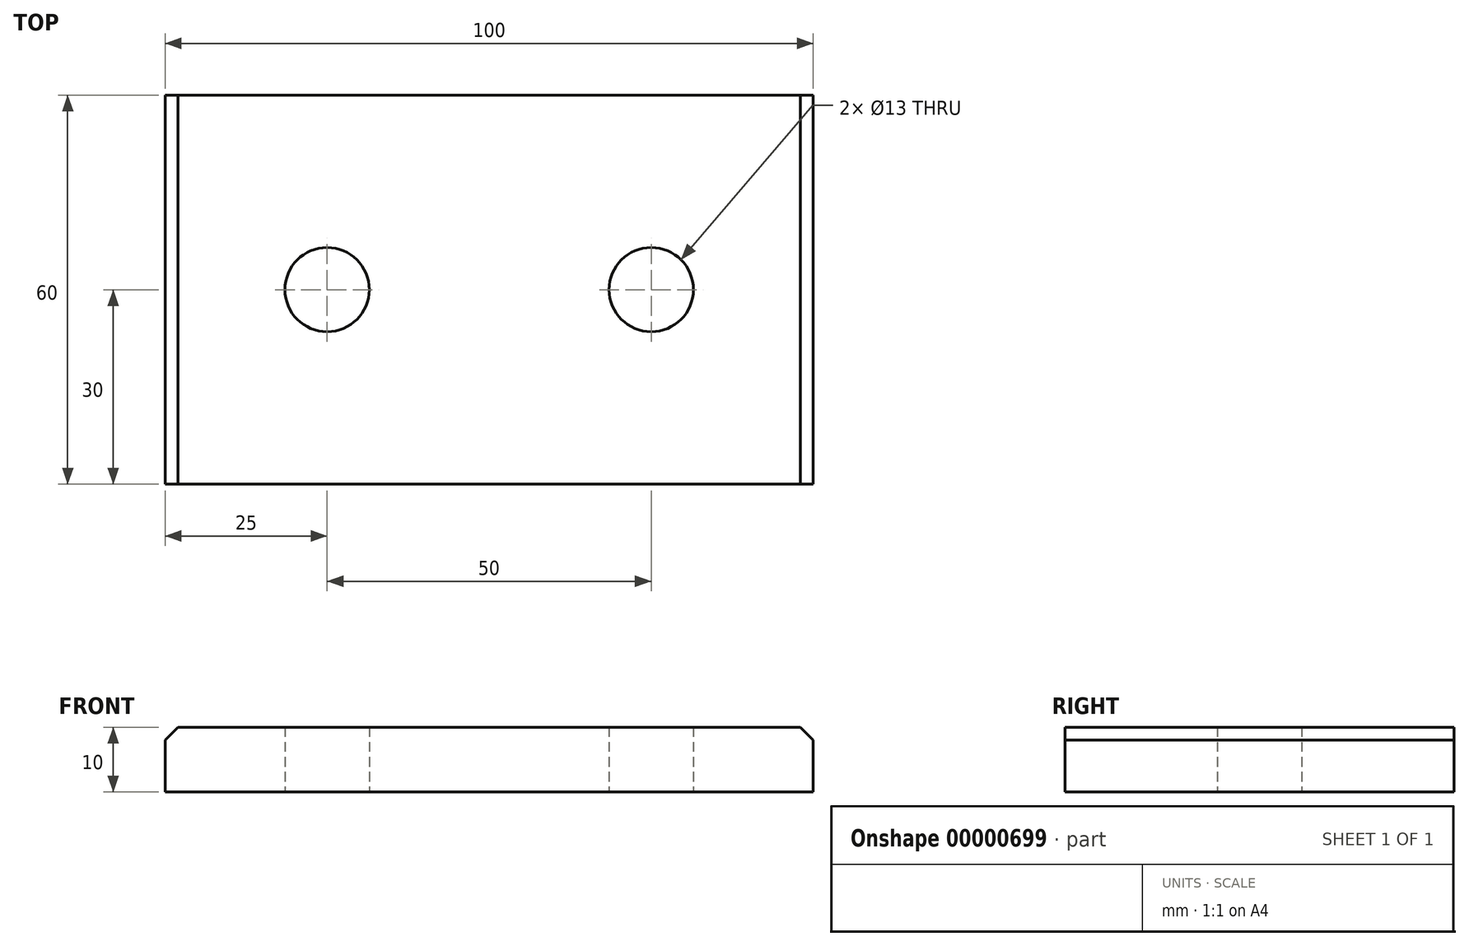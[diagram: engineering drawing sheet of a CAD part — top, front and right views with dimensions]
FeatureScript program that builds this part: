
annotation { "Feature Type Name" : "Feature", "Feature Type Description" : "" }
export const myFeature = defineFeature(function(context is Context, id is Id, definition is map)
    precondition{}
    {
        {
            var Q0;
            Q0=qCreatedBy(makeId("Top.planeOp"),FACE);
            var sketch = newSketch(context, id + "F0", { "sketchPlane" : qUnion([Q0])});
            skLineSegment(sketch, "E0.rect.bottom", {"start": v(-50, 30) * mm, "end": v(50, 30) * mm});
            skLineSegment(sketch, "E0.rect.top", {"start": v(-50, -30) * mm, "end": v(50, -30) * mm});
            skLineSegment(sketch, "E0.rect.left", {"start": v(-50, 30) * mm, "end": v(-50, -30) * mm});
            skLineSegment(sketch, "E0.rect.right", {"start": v(50, 30) * mm, "end": v(50, -30) * mm});
            skPoint(sketch, "E0.rect.middle", {"position": v(0, 0) * mm});
            skCircle(sketch, "E1", {"center": v(-25, 0) * mm, "radius": 6.5 * mm});
            skLineSegment(sketch, "E2", {"start": v(0, 30) * mm, "end": v(0, -30) * mm, "construction": true});
            skCircle(sketch, "E3.0.MirrorC", {"center": v(25, 0) * mm, "radius": 6.5 * mm});
            skSolve(sketch);
        }
        {
            var Q0;
            Q0=makeQuery(id+"F0.imprint","IMPRINT",FACE,{"disambiguationData":[TD([[makeQuery(id+"F0.imprint","IMPRINT",EDGE,{"derivedFrom":sQuery(id+"F0.wireOp",EDGE,"E0.rect.bottom")}),-1.0]])]});
            extrude(context, id + "F1", {"entities" : qUnion([Q0]), "endBound" : BoundingType.SYMMETRIC, "depth" : 10 * mm});
        }
        {
            var Q0;
            Q0=makeQuery(id+"F1.opExtrude","CAP_EDGE",EDGE,{"disambiguationData":[OSD([sQuery(id+"F0.wireOp",EDGE,"E0.rect.right")])],"isStart":false});
            var Q1;
            Q1=makeQuery(id+"F1.opExtrude","CAP_EDGE",EDGE,{"disambiguationData":[OSD([sQuery(id+"F0.wireOp",EDGE,"E0.rect.left")])],"isStart":false});
            chamfer(context, id + "F2", {"entities" : qUnion([Q0, Q1]), "width" : 2 * mm, "tangentPropagation" : true});
        }
    });
